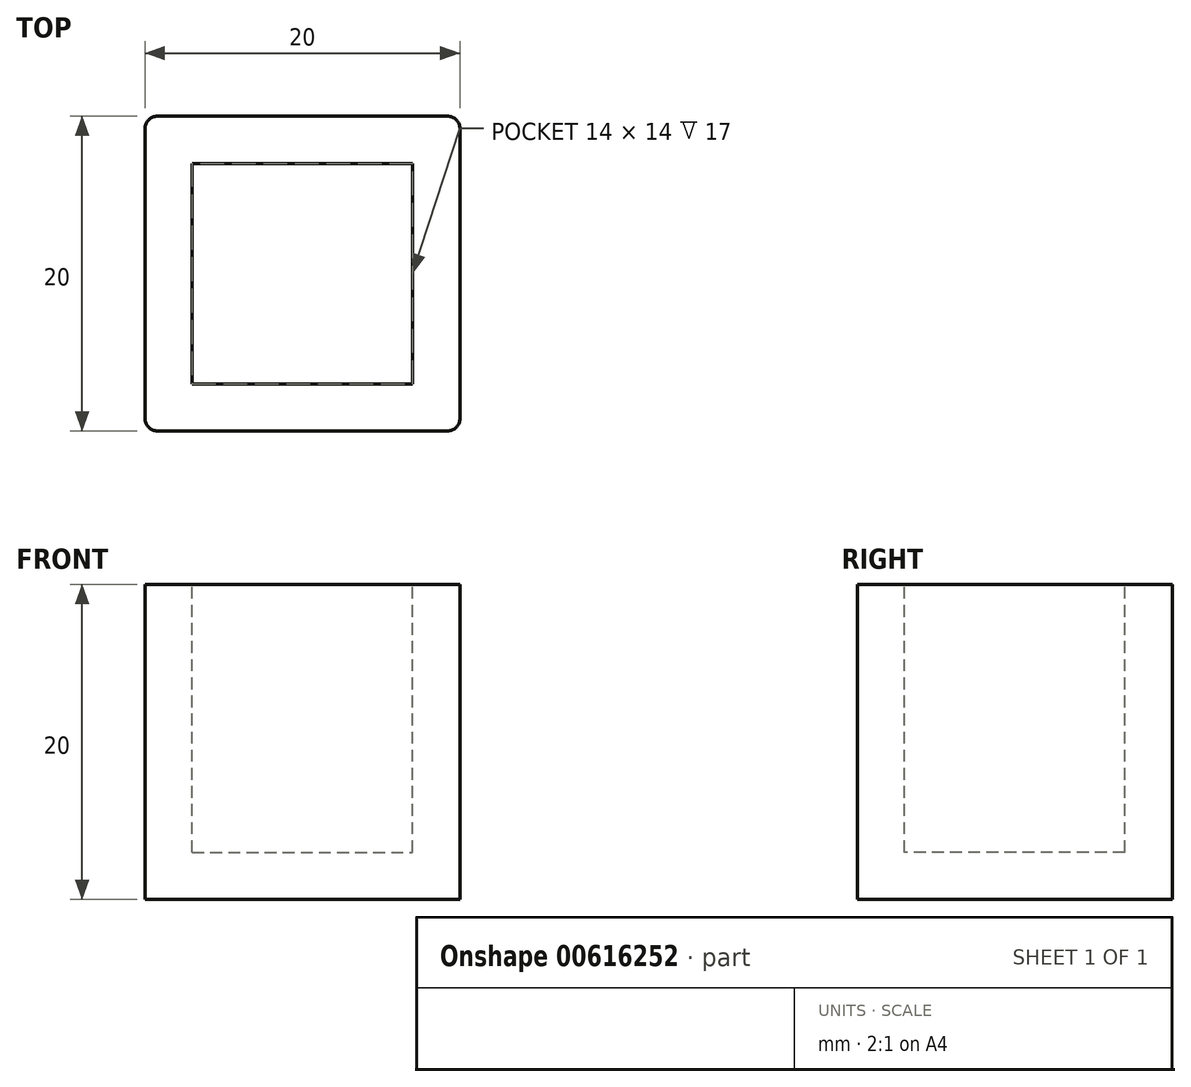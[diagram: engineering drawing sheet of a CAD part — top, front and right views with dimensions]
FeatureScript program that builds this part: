
annotation { "Feature Type Name" : "Feature", "Feature Type Description" : "" }
export const myFeature = defineFeature(function(context is Context, id is Id, definition is map)
    precondition{}
    {
        {
            var Q0;
            Q0=qCreatedBy(makeId("Top.planeOp"),FACE);
            var sketch = newSketch(context, id + "F0", { "sketchPlane" : qUnion([Q0])});
            skLineSegment(sketch, "E0.bottom", {"start": v(-10, 10) * mm, "end": v(10, 10) * mm});
            skLineSegment(sketch, "E0.top", {"start": v(-10, -10) * mm, "end": v(10, -10) * mm});
            skLineSegment(sketch, "E0.left", {"start": v(-10, 10) * mm, "end": v(-10, -10) * mm});
            skLineSegment(sketch, "E0.right", {"start": v(10, 10) * mm, "end": v(10, -10) * mm});
            skSolve(sketch);
        }
        {
            var Q0;
            Q0=makeQuery(id+"F0.imprint","IMPRINT",FACE,{"disambiguationData":[TD([[makeQuery(id+"F0.imprint","IMPRINT",EDGE,{"derivedFrom":sQuery(id+"F0.wireOp",EDGE,"E0.bottom")}),-1.0]])]});
            extrude(context, id + "F1", {"entities" : qUnion([Q0]), "depth" : 20 * mm, "offsetDistance" : 25 * mm});
        }
        {
            var Q0;
            Q0=makeQuery(id+"F1.opExtrude","SWEPT_EDGE",EDGE,{"disambiguationData":[OSD([sQuery(id+"F0.wireOp",EDGE,"E0.top"),sQuery(id+"F0.wireOp",EDGE,"E0.left")])]});
            var Q1;
            Q1=makeQuery(id+"F1.opExtrude","SWEPT_EDGE",EDGE,{"disambiguationData":[OSD([sQuery(id+"F0.wireOp",EDGE,"E0.top"),sQuery(id+"F0.wireOp",EDGE,"E0.right")])]});
            var Q2;
            Q2=makeQuery(id+"F1.opExtrude","SWEPT_EDGE",EDGE,{"disambiguationData":[OSD([sQuery(id+"F0.wireOp",EDGE,"E0.bottom"),sQuery(id+"F0.wireOp",EDGE,"E0.right")])]});
            var Q3;
            Q3=makeQuery(id+"F1.opExtrude","SWEPT_EDGE",EDGE,{"disambiguationData":[OSD([sQuery(id+"F0.wireOp",EDGE,"E0.bottom"),sQuery(id+"F0.wireOp",EDGE,"E0.left")])]});
            fillet(context, id + "F2", {"entities" : qUnion([Q0, Q1, Q2, Q3]), "radius" : 0.8 * mm, "tangentPropagation" : true, "allowEdgeOverflow" : false});
        }
        {
            var Q0;
            Q0=makeQuery(id+"F1.opExtrude","CAP_FACE",FACE,{"disambiguationData":[OSD([sQuery(id+"F0.wireOp",EDGE,"E0.bottom"),sQuery(id+"F0.wireOp",EDGE,"E0.top"),sQuery(id+"F0.wireOp",EDGE,"E0.left"),sQuery(id+"F0.wireOp",EDGE,"E0.right")])],"isStart":false});
            shell(context, id + "F3", {"entities" : qUnion([Q0]), "thickness" : 3 * mm});
        }
    });
